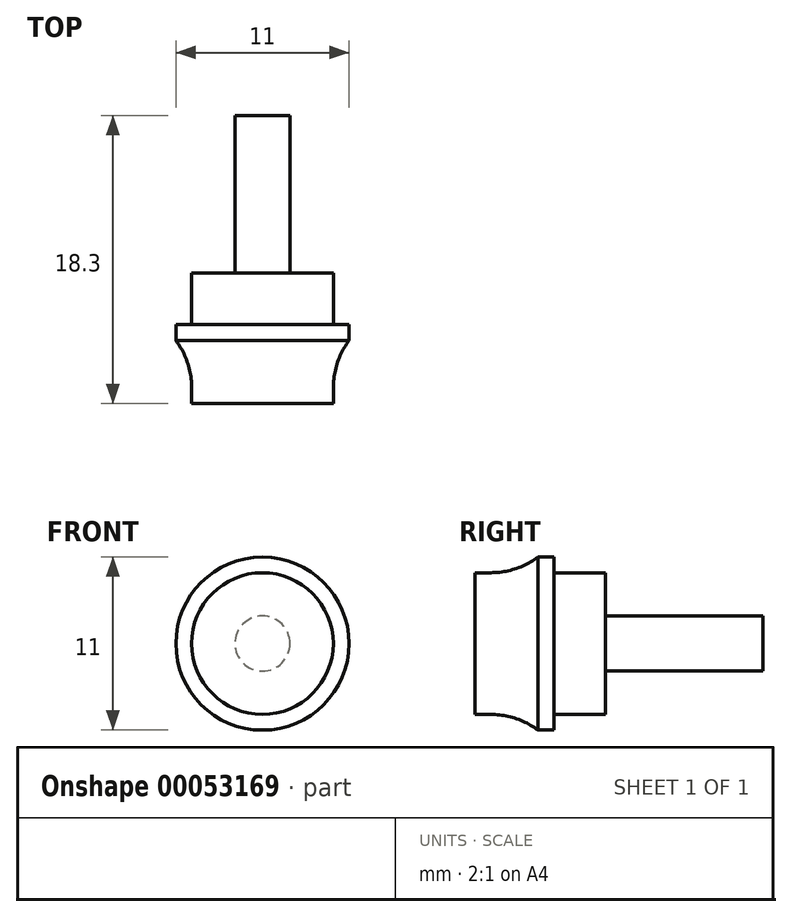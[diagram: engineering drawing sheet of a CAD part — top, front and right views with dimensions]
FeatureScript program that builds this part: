
annotation { "Feature Type Name" : "Feature", "Feature Type Description" : "" }
export const myFeature = defineFeature(function(context is Context, id is Id, definition is map)
    precondition{}
    {
        {
            var Q0;
            Q0=qCreatedBy(makeId("Front.planeOp"),FACE);
            var sketch = newSketch(context, id + "F0", { "sketchPlane" : qUnion([Q0])});
            skCircle(sketch, "E0", {"center": v(0, 0) * mm, "radius": 4.5 * mm});
            skSolve(sketch);
        }
        {
            var Q0;
            Q0=makeQuery(id+"F0.imprint","IMPRINT",FACE,{"disambiguationData":[TD([[makeQuery(id+"F0.imprint","IMPRINT",EDGE,{"derivedFrom":sQuery(id+"F0.wireOp",EDGE,"E0")}),1.0]])]});
            extrude(context, id + "F1", {"entities" : qUnion([Q0]), "depth" : 5 * mm});
        }
        {
            var Q0;
            Q0=makeQuery(id+"F1.opExtrude","CAP_FACE",FACE,{"disambiguationData":[OSD([sQuery(id+"F0.wireOp",EDGE,"E0")])],"isStart":true});
            extrude(context, id + "F2", {"entities" : qUnion([Q0]), "operationType" : NewBodyOperationType.ADD, "depth" : 3.3 * mm});
        }
        {
            var Q0;
            Q0=qCreatedBy(makeId("Front.planeOp"),FACE);
            var sketch = newSketch(context, id + "F3", { "sketchPlane" : qUnion([Q0])});
            skCircle(sketch, "E1", {"center": v(0, 0) * mm, "radius": 5.5 * mm});
            skSolve(sketch);
        }
        {
            var Q0;
            Q0=makeQuery(id+"F3.imprint","IMPRINT",FACE,{"disambiguationData":[TD([[makeQuery(id+"F3.imprint","IMPRINT",EDGE,{"derivedFrom":sQuery(id+"F3.wireOp",EDGE,"E1")}),1.0]])]});
            var Q1;
            Q1=sQuery(id+"F3.wireOp",EDGE,"E1");
            extrude(context, id + "F4", {"entities" : qUnion([Q0]), "operationType" : NewBodyOperationType.ADD, "surfaceEntities" : qUnion([Q1]), "depth" : 1 * mm});
        }
        {
            var Q0;
            {var subQ0=sQuery(id+"F0.wireOp",EDGE,"E0");Q0=makeQuery(id+"F4.boolean.opBoolean","INTERSECT",EDGE,{"derivedFrom":[makeQuery(id+"F2.boolean.opBoolean","MERGE",FACE,{"derivedFrom":[makeQuery(id+"F1.opExtrude","SWEPT_FACE",FACE,{"disambiguationData":[OSD([subQ0])]}),makeQuery(id+"F2.opExtrude","SWEPT_FACE",FACE,{"disambiguationData":[OSD([subQ0])]})]}),makeQuery(id+"F4.opExtrude","CAP_FACE",FACE,{"disambiguationData":[OSD([sQuery(id+"F3.wireOp",EDGE,"E1")])],"isStart":false})]});}
            fillet(context, id + "F5", {"entities" : qUnion([Q0]), "radius" : 5 * mm, "tangentPropagation" : true, "allowEdgeOverflow" : false});
        }
        {
            var Q0;
            Q0=makeQuery(id+"F2.opExtrude","CAP_FACE",FACE,{"disambiguationData":[OSD([sQuery(id+"F0.wireOp",EDGE,"E0")])],"isStart":false});
            var sketch = newSketch(context, id + "F6", { "sketchPlane" : qUnion([Q0])});
            skCircle(sketch, "E2", {"center": v(0, 0) * mm, "radius": 1.75 * mm});
            skSolve(sketch);
        }
        {
            var Q0;
            Q0=makeQuery(id+"F6.imprint","IMPRINT",FACE,{"disambiguationData":[TD([[makeQuery(id+"F6.imprint","IMPRINT",EDGE,{"derivedFrom":sQuery(id+"F6.wireOp",EDGE,"E2")}),1.0]])]});
            extrude(context, id + "F7", {"entities" : qUnion([Q0]), "operationType" : NewBodyOperationType.ADD, "depth" : 10 * mm});
        }
    });
